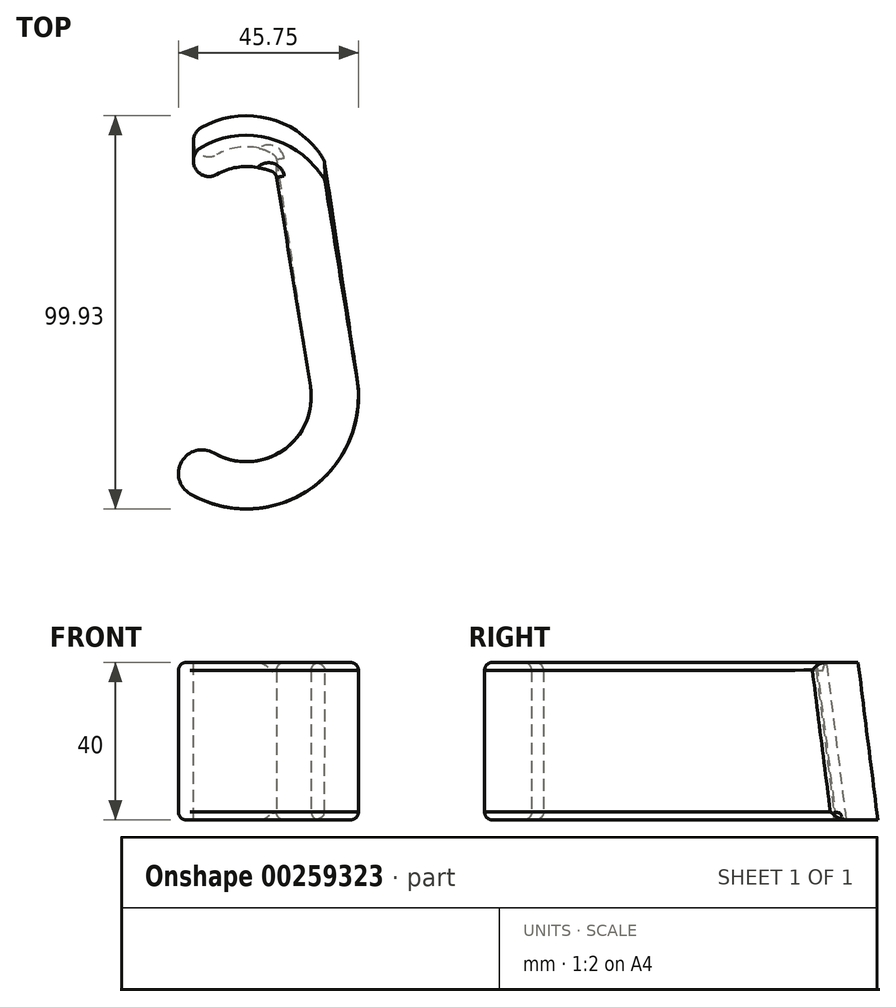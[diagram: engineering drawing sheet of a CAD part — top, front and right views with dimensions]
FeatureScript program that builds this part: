
annotation { "Feature Type Name" : "Feature", "Feature Type Description" : "" }
export const myFeature = defineFeature(function(context is Context, id is Id, definition is map)
    precondition{}
    {
        {
            var Q0;
            Q0=qCreatedBy(makeId("Right.planeOp"),FACE);
            var sketch = newSketch(context, id + "F0", { "sketchPlane" : qUnion([Q0])});
            skArc(sketch, "E0", {"start": v(2.66, 16.28) * mm, "mid": v(-13.58, 9.38) * mm, "end": v(-14.29, -8.25) * mm});
            skArc(sketch, "E1", {"start": v(56.5, -7.5) * mm, "mid": v(58.5, 0) * mm, "end": v(56.5, 7.5) * mm});
            skPoint(sketch, "E2", {"position": v(58.5, 0) * mm});
            skLineSegment(sketch, "E3", {"start": v(56.5, 7.5) * mm, "end": v(2.66, 16.28) * mm});
            skLineSegment(sketch, "E4", {"start": v(56.5, -7.5) * mm, "end": v(2.66, -16.28) * mm, "construction": true});
            skArc(sketch, "E5", {"start": v(-24.68, -14.25) * mm, "mid": v(-16.49, -16.45) * mm, "end": v(-14.29, -8.25) * mm});
            skLineSegment(sketch, "E6", {"start": v(0, 0) * mm, "end": v(-24.68, -14.25) * mm, "construction": true});
            skArc(sketch, "E7", {"start": v(-14.29, -8.25) * mm, "mid": v(-7.07, -14.9) * mm, "end": v(2.66, -16.28) * mm, "construction": true});
            skArc(sketch, "E8", {"start": v(4.59, 28.13) * mm, "mid": v(-23.45, 16.2) * mm, "end": v(-24.68, -14.25) * mm});
            skLineSegment(sketch, "E9", {"start": v(0, 0) * mm, "end": v(4.59, 28.13) * mm, "construction": true});
            skLineSegment(sketch, "E10", {"start": v(4.59, 28.13) * mm, "end": v(54.93, 19.91) * mm});
            skArc(sketch, "E11", {"start": v(54.93, 19.91) * mm, "mid": v(65.64, 5.98) * mm, "end": v(63.38, -11.45) * mm});
            skPoint(sketch, "E12", {"position": v(66.43, 0) * mm});
            skLineSegment(sketch, "E13", {"start": v(43.44, 0) * mm, "end": v(63.38, -11.45) * mm, "construction": true});
            skArc(sketch, "E14", {"start": v(56.5, -7.5) * mm, "mid": v(57.96, -12.91) * mm, "end": v(63.38, -11.45) * mm});
            skLineSegment(sketch, "E15", {"start": v(66.43, 0) * mm, "end": v(-28.5, 0) * mm, "construction": true});
            skSolve(sketch);
        }
        {
            var Q0;
            Q0=qCreatedBy(makeId("Right.planeOp"),FACE);
            cPlane(context, id + "F1", {"entities" : qUnion([Q0]), "cplaneType" : CPlaneType.OFFSET, "offset" : 40 * mm, "width" : 150 * mm, "height" : 150 * mm});
        }
        {
            var Q0;
            Q0=qCreatedBy(id+"F1.planeOp",FACE);
            var sketch = newSketch(context, id + "F2", { "sketchPlane" : qUnion([Q0])});
            skArc(sketch, "E16", {"start": v(2.44, 16.32) * mm, "mid": v(-13.64, 9.29) * mm, "end": v(-14.29, -8.25) * mm});
            skArc(sketch, "E17", {"start": v(61.5, -7.5) * mm, "mid": v(63.5, 0) * mm, "end": v(61.5, 7.5) * mm});
            skPoint(sketch, "E18", {"position": v(63.5, 0) * mm});
            skLineSegment(sketch, "E19", {"start": v(61.5, 7.5) * mm, "end": v(2.44, 16.32) * mm});
            skLineSegment(sketch, "E20", {"start": v(61.5, -7.5) * mm, "end": v(2.44, -16.32) * mm, "construction": true});
            skArc(sketch, "E21", {"start": v(-24.68, -14.25) * mm, "mid": v(-16.49, -16.45) * mm, "end": v(-14.29, -8.25) * mm});
            skLineSegment(sketch, "E22", {"start": v(0, 0) * mm, "end": v(-24.68, -14.25) * mm, "construction": true});
            skArc(sketch, "E23", {"start": v(-14.29, -8.25) * mm, "mid": v(-7.17, -14.86) * mm, "end": v(2.44, -16.32) * mm, "construction": true});
            skArc(sketch, "E24", {"start": v(4.2, 28.19) * mm, "mid": v(-23.56, 16.04) * mm, "end": v(-24.68, -14.25) * mm});
            skLineSegment(sketch, "E25", {"start": v(0, 0) * mm, "end": v(4.2, 28.19) * mm, "construction": true});
            skLineSegment(sketch, "E26", {"start": v(4.2, 28.19) * mm, "end": v(60.04, 19.85) * mm});
            skArc(sketch, "E27", {"start": v(60.04, 19.85) * mm, "mid": v(70.66, 5.92) * mm, "end": v(68.38, -11.45) * mm});
            skPoint(sketch, "E28", {"position": v(71.43, 0) * mm});
            skLineSegment(sketch, "E29", {"start": v(48.44, 0) * mm, "end": v(68.38, -11.45) * mm, "construction": true});
            skArc(sketch, "E30", {"start": v(61.5, -7.5) * mm, "mid": v(62.96, -12.91) * mm, "end": v(68.38, -11.45) * mm});
            skLineSegment(sketch, "E31", {"start": v(71.43, 0) * mm, "end": v(-28.5, 0) * mm, "construction": true});
            skSolve(sketch);
        }
        {
            var Q0;
            Q0=makeQuery(id+"F0.imprint","IMPRINT",FACE,{"disambiguationData":[TD([[makeQuery(id+"F0.imprint","IMPRINT",EDGE,{"derivedFrom":sQuery(id+"F0.wireOp",EDGE,"E0")}),-1.0]])]});
            var Q1;
            Q1=makeQuery(id+"F2.imprint","IMPRINT",FACE,{"disambiguationData":[TD([[makeQuery(id+"F2.imprint","IMPRINT",EDGE,{"derivedFrom":sQuery(id+"F2.wireOp",EDGE,"E16")}),-1.0]])]});
            loft(context, id + "F3", {"sheetProfilesArray" : [{ "sheetProfileEntities" : qUnion([Q0]) }, { "sheetProfileEntities" : qUnion([Q1]) }]});
        }
        {
            var Q0;
            Q0=makeQuery(id+"F3.opLoft","SWEPT_EDGE",EDGE,{"disambiguationData":[OSD([sQuery(id+"F0.wireOp",EDGE,"E1"),sQuery(id+"F0.wireOp",EDGE,"E3"),sQuery(id+"F2.wireOp",EDGE,"E17"),sQuery(id+"F2.wireOp",EDGE,"E19")])]});
            var Q1;
            Q1=makeQuery(id+"F3.opLoft","SWEPT_EDGE",EDGE,{"disambiguationData":[OSD([sQuery(id+"F0.wireOp",EDGE,"E10"),sQuery(id+"F0.wireOp",EDGE,"E11"),sQuery(id+"F2.wireOp",EDGE,"E26"),sQuery(id+"F2.wireOp",EDGE,"E27")])]});
            var Q2;
            Q2=makeQuery(id+"F3.opLoft","MID_CAP_EDGE",EDGE,{"disambiguationData":[OSD([sQuery(id+"F2.wireOp",EDGE,"E21"),sQuery(id+"F2.wireOp",EDGE,"E24"),sQuery(id+"F2.wireOp",EDGE,"E26")])],"capPos":1.0});
            var Q3;
            Q3=makeQuery(id+"F3.opLoft","MID_CAP_EDGE",EDGE,{"disambiguationData":[OSD([sQuery(id+"F0.wireOp",EDGE,"E5"),sQuery(id+"F0.wireOp",EDGE,"E8"),sQuery(id+"F0.wireOp",EDGE,"E10")])],"capPos":0.0});
            fillet(context, id + "F4", {"entities" : qUnion([Q0, Q1, Q2, Q3]), "radius" : 2 * mm, "tangentPropagation" : true, "allowEdgeOverflow" : false});
        }
        {
            var Q0;
            Q0=makeQuery(id+"F3.opLoft","SWEPT_BODY",BODY,{"disambiguationData":[OSD([makeQuery(id+"F0.imprint","IMPRINT",FACE,{"disambiguationData":[TD([[makeQuery(id+"F0.imprint","IMPRINT",EDGE,{"derivedFrom":sQuery(id+"F0.wireOp",EDGE,"E0")}),-1.0]])]}),makeQuery(id+"F2.imprint","IMPRINT",FACE,{"disambiguationData":[TD([[makeQuery(id+"F2.imprint","IMPRINT",EDGE,{"derivedFrom":sQuery(id+"F2.wireOp",EDGE,"E16")}),-1.0]])]})])]});
            var Q1;
            Q1=sQuery(id+"F2.wireOp",EDGE,"E31");
            transform(context, id + "F5", {"entities" : qUnion([Q0]), "transformType" : TransformType.ROTATION, "transformAxis" : qUnion([Q1]), "angle" : 90 * degree, "oppositeDirection" : true, "makeCopy" : false});
        }
    });
